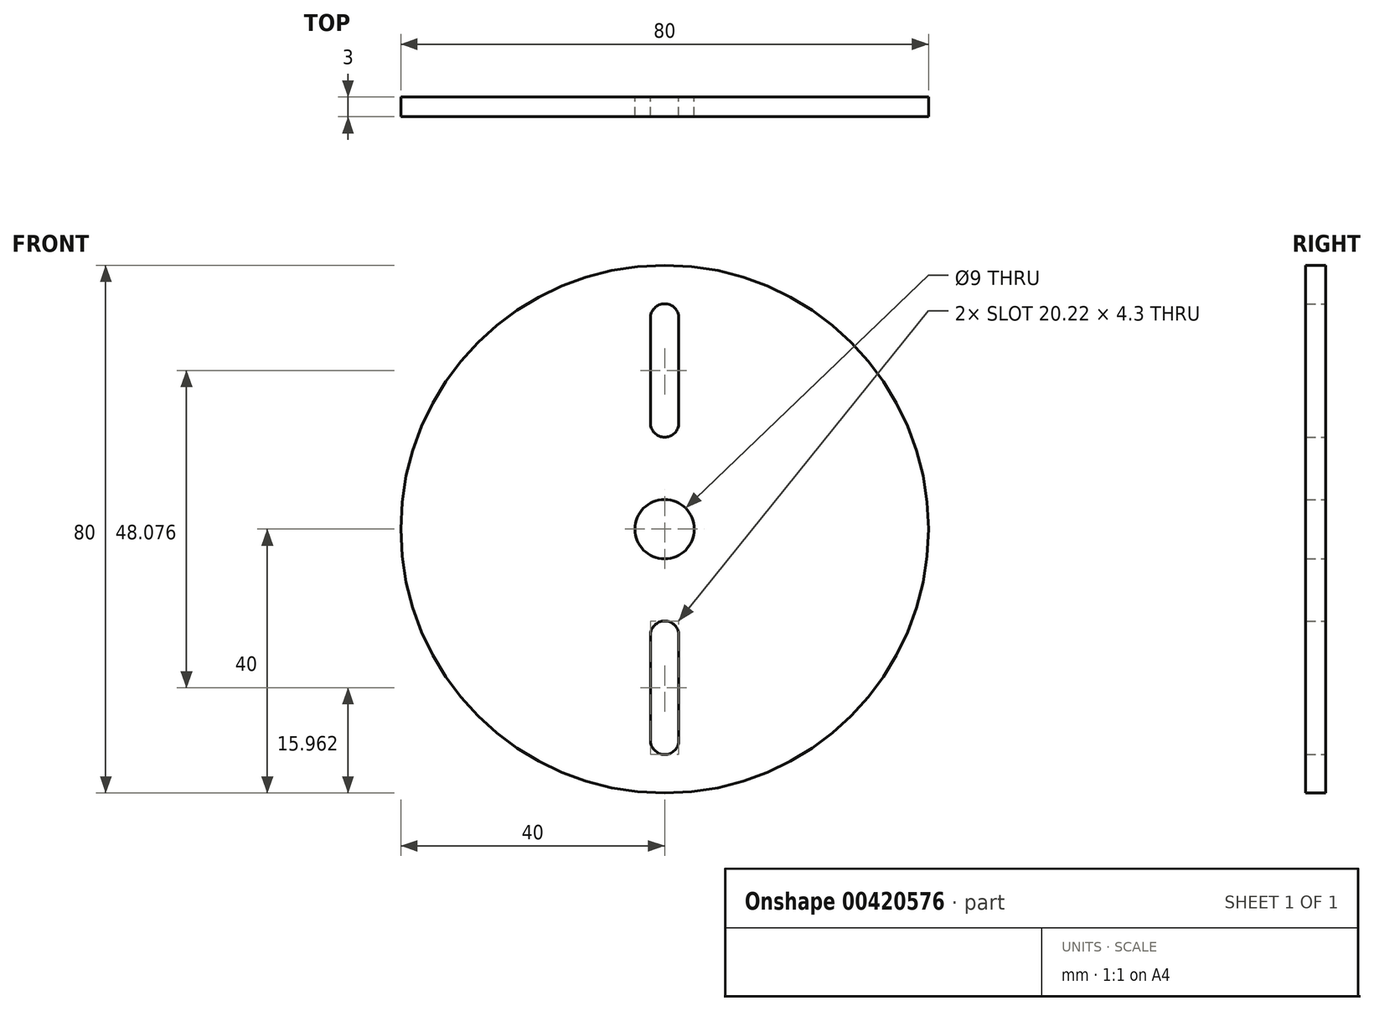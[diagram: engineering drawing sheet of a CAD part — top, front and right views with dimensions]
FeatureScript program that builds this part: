
annotation { "Feature Type Name" : "Feature", "Feature Type Description" : "" }
export const myFeature = defineFeature(function(context is Context, id is Id, definition is map)
    precondition{}
    {
        {
            var Q0;
            Q0=qCreatedBy(makeId("Front.planeOp"),FACE);
            var sketch = newSketch(context, id + "F0", { "sketchPlane" : qUnion([Q0])});
            skCircle(sketch, "E0", {"center": v(0, 0) * mm, "radius": 40 * mm});
            skCircle(sketch, "E1", {"center": v(0, 0) * mm, "radius": 4.5 * mm});
            skLineSegment(sketch, "E2", {"start": v(0, 32) * mm, "end": v(0, 16.08) * mm});
            skLineSegment(sketch, "E3.MirrorCS", {"start": v(0, -32) * mm, "end": v(0, -16.08) * mm});
            skArc(sketch, "E4.0.startCap", {"start": v(-2.15, 32) * mm, "mid": v(0, 34.15) * mm, "end": v(2.15, 32) * mm});
            skArc(sketch, "E4.0.endCap", {"start": v(2.15, 16.08) * mm, "mid": v(0, 13.93) * mm, "end": v(-2.15, 16.08) * mm});
            skLineSegment(sketch, "E4.0.left", {"start": v(2.15, 32) * mm, "end": v(2.15, 16.08) * mm});
            skLineSegment(sketch, "E4.0.right", {"start": v(-2.15, 32) * mm, "end": v(-2.15, 16.08) * mm});
            skLineSegment(sketch, "E5.MirrorCS", {"start": v(-2.15, -32) * mm, "end": v(-2.15, -16.08) * mm});
            skArc(sketch, "E6.MirrorCS", {"start": v(-2.15, -32) * mm, "mid": v(0, -34.15) * mm, "end": v(2.15, -32) * mm});
            skArc(sketch, "E7.MirrorCS", {"start": v(2.15, -16.08) * mm, "mid": v(0, -13.93) * mm, "end": v(-2.15, -16.08) * mm});
            skLineSegment(sketch, "E8.MirrorCS", {"start": v(2.15, -32) * mm, "end": v(2.15, -16.08) * mm});
            skSolve(sketch);
        }
        {
            var Q0;
            Q0=makeQuery(id+"F0.imprint","IMPRINT",FACE,{"disambiguationData":[TD([[makeQuery(id+"F0.imprint","IMPRINT",EDGE,{"derivedFrom":sQuery(id+"F0.wireOp",EDGE,"E0")}),1.0]])]});
            extrude(context, id + "F1", {"entities" : qUnion([Q0]), "depth" : 3 * mm});
        }
    });
